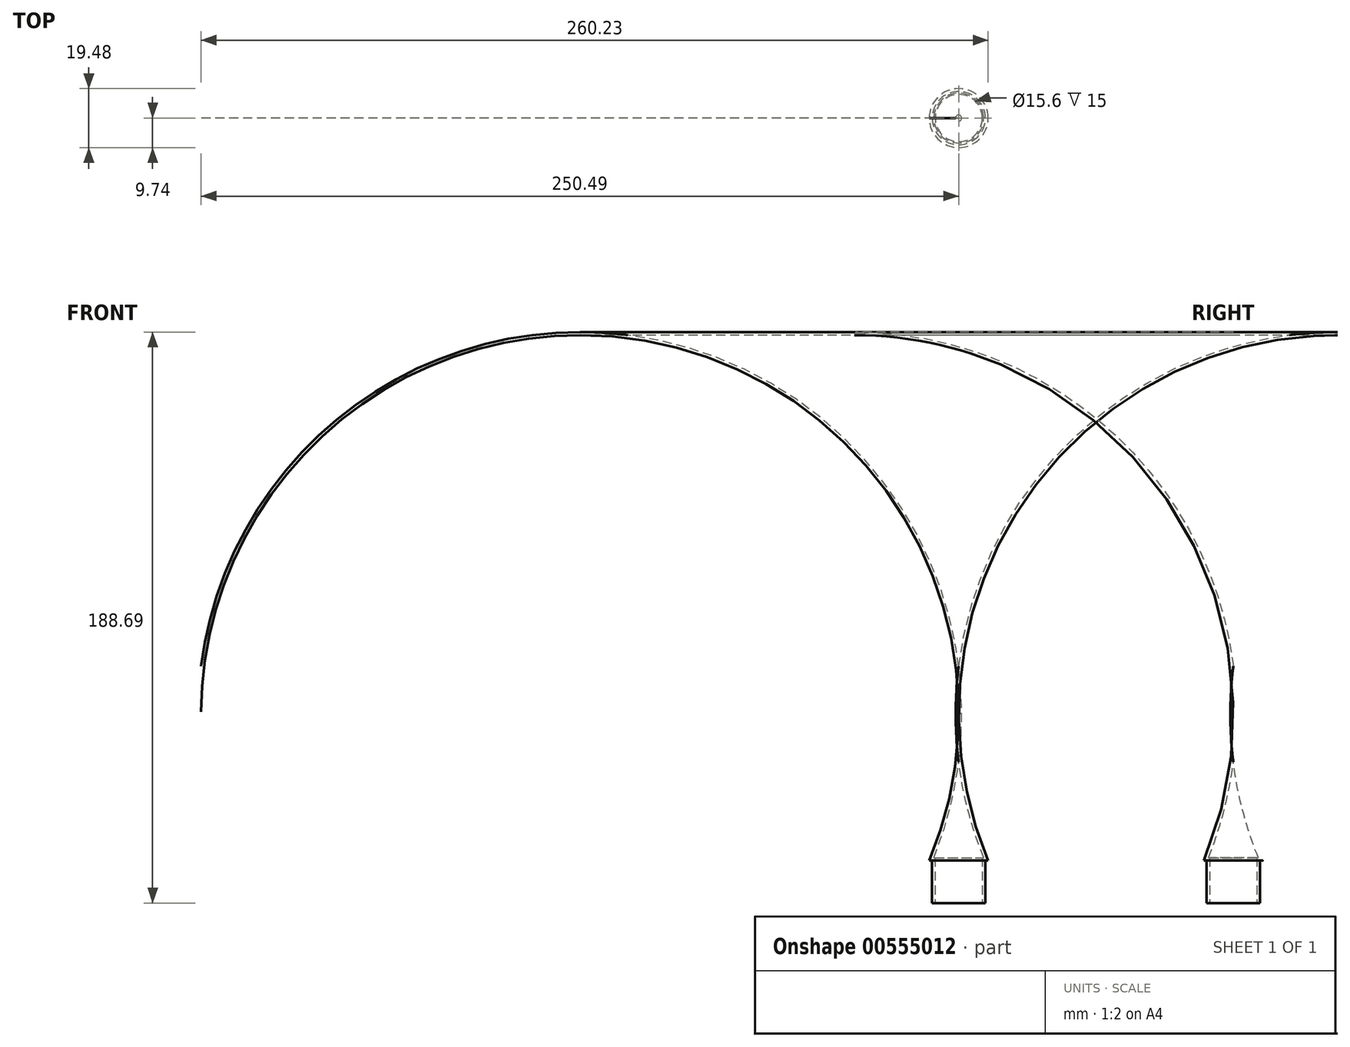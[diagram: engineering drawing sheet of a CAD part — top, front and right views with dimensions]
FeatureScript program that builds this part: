
annotation { "Feature Type Name" : "Feature", "Feature Type Description" : "" }
export const myFeature = defineFeature(function(context is Context, id is Id, definition is map)
    precondition{}
    {
        {
            var Q0;
            Q0=qCreatedBy(makeId("Front.planeOp"),FACE);
            var sketch = newSketch(context, id + "F0", { "sketchPlane" : qUnion([Q0])});
            skLineSegment(sketch, "E0", {"start": v(0, 0) * mm, "end": v(0, 63.2) * mm});
            skLineSegment(sketch, "E1", {"start": v(7.8, 0) * mm, "end": v(8.8, 0) * mm});
            skLineSegment(sketch, "E2", {"start": v(7.8, 0) * mm, "end": v(7.8, 15) * mm});
            skLineSegment(sketch, "E3", {"start": v(7.8, 15) * mm, "end": v(8.25, 15) * mm});
            skArc(sketch, "E4", {"start": v(0, 46.56) * mm, "mid": v(3.1, 30.51) * mm, "end": v(8.25, 15) * mm});
            skLineSegment(sketch, "E5.0", {"start": v(8.8, 0) * mm, "end": v(8.8, 14) * mm});
            skLineSegment(sketch, "E5.1", {"start": v(8.8, 14) * mm, "end": v(9.74, 14) * mm});
            skArc(sketch, "E5.2", {"start": v(0, 63.2) * mm, "mid": v(2.38, 38.1) * mm, "end": v(9.74, 14) * mm});
            skSolve(sketch);
        }
        {
            var Q0;
            Q0=makeQuery(id+"F0.imprint","IMPRINT",FACE,{"disambiguationData":[TD([[makeQuery(id+"F0.imprint","IMPRINT",EDGE,{"derivedFrom":sQuery(id+"F0.wireOp",EDGE,"E1")}),1.0]])]});
            var Q1;
            Q1=sQuery(id+"F0.wireOp",EDGE,"E0");
            revolve(context, id + "F1", {"entities" : qUnion([Q0]), "axis" : qUnion([Q1]), "revolveType" : RevolveType.FULL});
        }
    });
